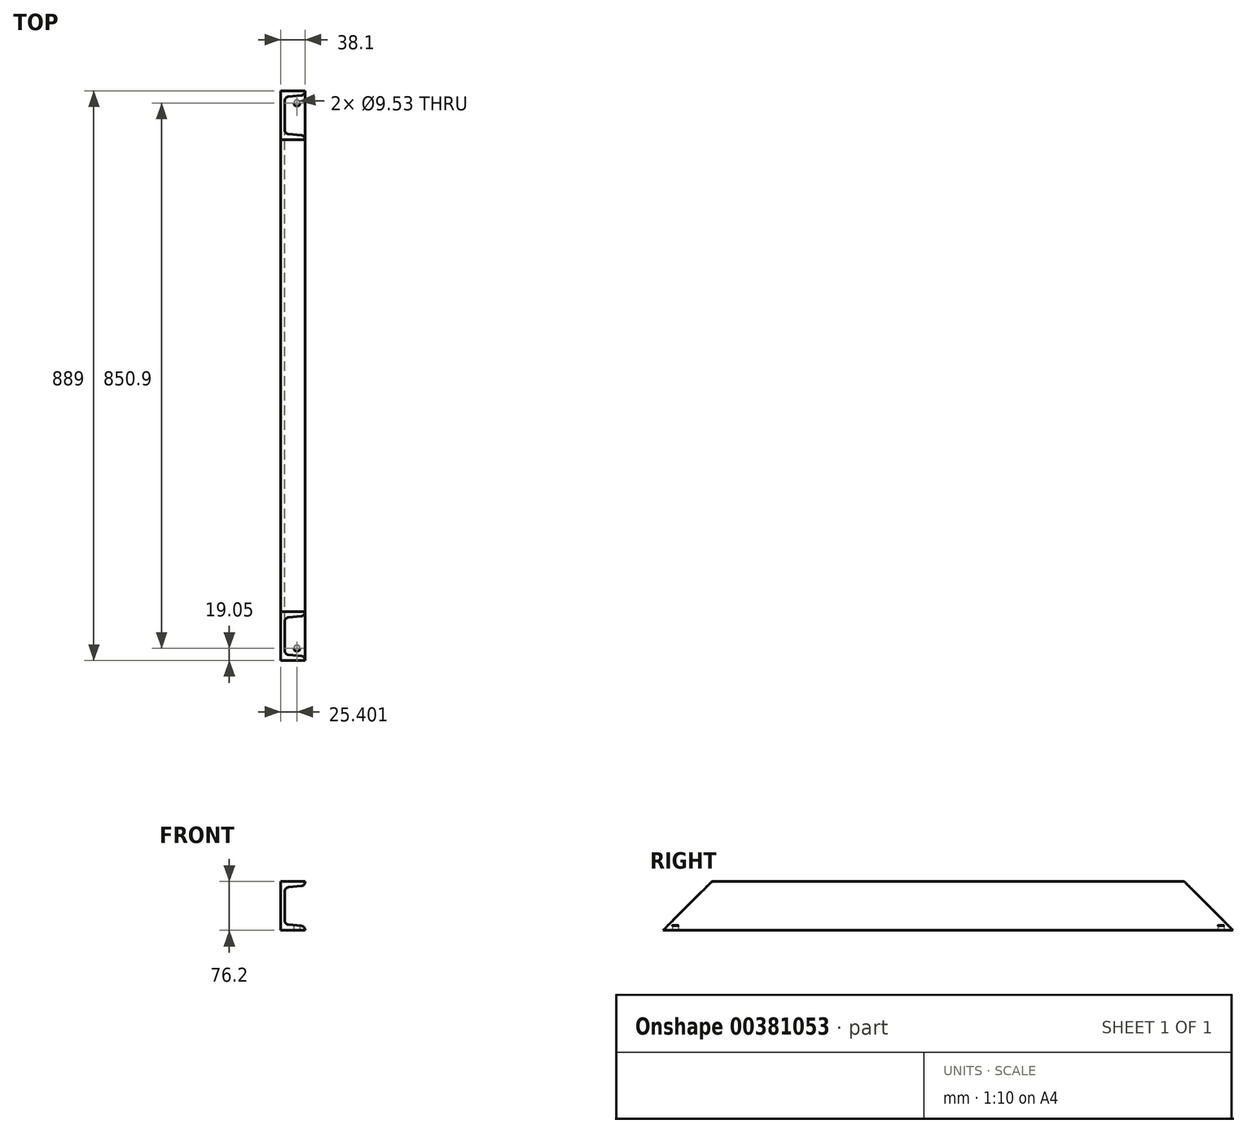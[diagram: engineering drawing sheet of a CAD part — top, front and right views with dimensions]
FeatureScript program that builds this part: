
annotation { "Feature Type Name" : "Feature", "Feature Type Description" : "" }
export const myFeature = defineFeature(function(context is Context, id is Id, definition is map)
    precondition{}
    {
        {
            var Q0;
            Q0=qCreatedBy(makeId("Front.planeOp"),FACE);
            var sketch = newSketch(context, id + "F0", { "sketchPlane" : qUnion([Q0])});
            skLineSegment(sketch, "E0", {"start": v(-3.43, 34.47) * mm, "end": v(-3.43, -41.73) * mm});
            skLineSegment(sketch, "E1", {"start": v(-3.43, 34.47) * mm, "end": v(34.67, 34.47) * mm});
            skLineSegment(sketch, "E2", {"start": v(34.67, -41.73) * mm, "end": v(34.67, -41.13) * mm});
            skLineSegment(sketch, "E3", {"start": v(28.95, -34.8) * mm, "end": v(8.64, -32.78) * mm});
            skLineSegment(sketch, "E4", {"start": v(2.92, -26.46) * mm, "end": v(2.92, 19.2) * mm});
            skLineSegment(sketch, "E5", {"start": v(8.64, 25.52) * mm, "end": v(28.95, 27.55) * mm});
            skLineSegment(sketch, "E6", {"start": v(34.67, 34.47) * mm, "end": v(34.67, 33.87) * mm});
            skLineSegment(sketch, "E7", {"start": v(-3.43, -41.73) * mm, "end": v(34.67, -41.73) * mm});
            skPoint(sketch, "E8.visualSharp", {"position": v(34.67, -35.38) * mm});
            skArc(sketch, "E8.filletArc", {"start": v(34.67, -41.13) * mm, "mid": v(33.03, -36.86) * mm, "end": v(28.95, -34.8) * mm});
            skPoint(sketch, "E9.visualSharp", {"position": v(34.67, 28.12) * mm});
            skArc(sketch, "E9.filletArc", {"start": v(28.95, 27.55) * mm, "mid": v(33.03, 29.6) * mm, "end": v(34.67, 33.87) * mm});
            skPoint(sketch, "E10.visualSharp", {"position": v(2.92, -32.2) * mm});
            skArc(sketch, "E10.filletArc", {"start": v(2.92, -26.46) * mm, "mid": v(4.56, -30.72) * mm, "end": v(8.64, -32.78) * mm});
            skPoint(sketch, "E11.visualSharp", {"position": v(2.92, 24.95) * mm});
            skArc(sketch, "E11.filletArc", {"start": v(8.64, 25.52) * mm, "mid": v(4.56, 23.46) * mm, "end": v(2.92, 19.2) * mm});
            skPoint(sketch, "E12", {"position": v(-0.25, -0.22) * mm});
            skSolve(sketch);
        }
        {
            var Q0;
            Q0 = qSketchRegion(id + "F0", true);
            extrude(context, id + "F1", {"entities" : qUnion([Q0]), "depth" : 889 * mm, "symmetric" : true});
        }
        {
            var Q0;
            Q0=makeQuery(id+"F1.opExtrude","CAP_EDGE",EDGE,{"disambiguationData":[OSD([sQuery(id+"F0.wireOp",EDGE,"E1")])],"isStart":false});
            chamfer(context, id + "F2", {"entities" : qUnion([Q0]), "width" : 76.2 * mm, "tangentPropagation" : true});
        }
        {
            var Q0;
            Q0=makeQuery(id+"F1.opExtrude","CAP_EDGE",EDGE,{"disambiguationData":[OSD([sQuery(id+"F0.wireOp",EDGE,"E1")])],"isStart":true});
            chamfer(context, id + "F3", {"entities" : qUnion([Q0]), "width" : 76.2 * mm, "tangentPropagation" : true});
        }
        {
            var Q0;
            Q0=makeQuery(id+"F1.opExtrude","SWEPT_FACE",FACE,{"disambiguationData":[OSD([sQuery(id+"F0.wireOp",EDGE,"E7")])]});
            var sketch = newSketch(context, id + "F4", { "sketchPlane" : qUnion([Q0])});
            skCircle(sketch, "E13", {"center": v(21.97, 425.45) * mm, "radius": 4.76 * mm});
            skCircle(sketch, "E14.MirrorC", {"center": v(21.97, -425.45) * mm, "radius": 4.76 * mm});
            skSolve(sketch);
        }
        {
            var Q0;
            Q0=makeQuery(id+"F4.imprint","IMPRINT",FACE,{"disambiguationData":[TD([[makeQuery(id+"F4.imprint","IMPRINT",EDGE,{"derivedFrom":sQuery(id+"F4.wireOp",EDGE,"E13")}),1.0]])]});
            extrude(context, id + "F5", {"entities" : qUnion([Q0]), "operationType" : NewBodyOperationType.REMOVE, "oppositeDirection" : true, "depth" : 25.4 * mm});
        }
        {
            var Q0;
            Q0 = qSketchRegion(id + "F4", true);
            extrude(context, id + "F6", {"entities" : qUnion([Q0]), "operationType" : NewBodyOperationType.REMOVE, "oppositeDirection" : true, "depth" : 25.4 * mm});
        }
    });
